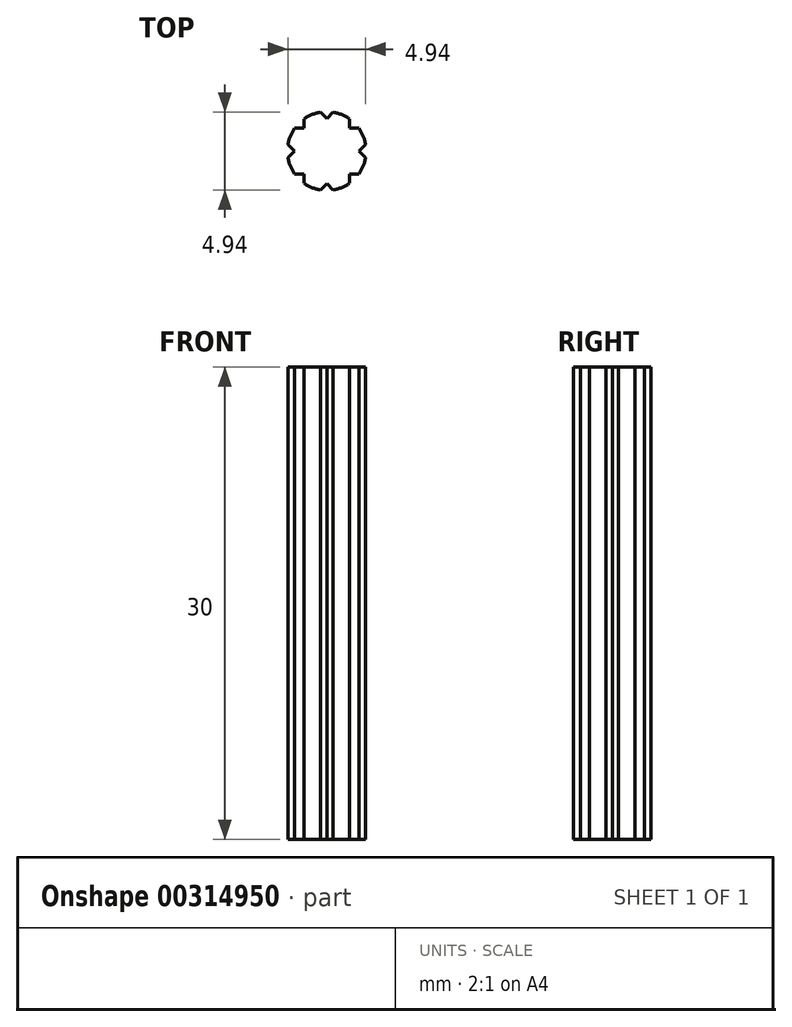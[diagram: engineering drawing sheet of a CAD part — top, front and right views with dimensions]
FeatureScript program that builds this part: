
annotation { "Feature Type Name" : "Feature", "Feature Type Description" : "" }
export const myFeature = defineFeature(function(context is Context, id is Id, definition is map)
    precondition{}
    {
        {
            assignVariable(context, id + "F0", {"name" : "height", "anyValue" : 30});
        }
        {
            assignVariable(context, id + "F1", {"name" : "notches", "anyValue" : 8});
        }
        {
            var Q0;
            Q0=qCreatedBy(makeId("Top.planeOp"),FACE);
            var sketch = newSketch(context, id + "F2", { "sketchPlane" : qUnion([Q0])});
            skCircle(sketch, "E0", {"center": v(0, 0) * mm, "radius": 2.5 * mm});
            skLineSegment(sketch, "E1", {"start": v(0, 0) * mm, "end": v(0, 2.5) * mm, "construction": true});
            skPoint(sketch, "E2.middle", {"position": v(0, 2.5) * mm});
            skSolve(sketch);
        }
        {
            var Q0;
            Q0=qCreatedBy(makeId("Top.planeOp"),FACE);
            var sketch = newSketch(context, id + "F3", { "sketchPlane" : qUnion([Q0])});
            skCircle(sketch, "E3", {"center": v(0, 0) * mm, "radius": 2.5 * mm});
            skLineSegment(sketch, "E4", {"start": v(0, 0) * mm, "end": v(0, 2.5) * mm, "construction": true});
            skLineSegment(sketch, "E5.bottom", {"start": v(0.44, 2.5) * mm, "end": v(0, 2.06) * mm});
            skLineSegment(sketch, "E5.top", {"start": v(0, 2.94) * mm, "end": v(-0.44, 2.5) * mm});
            skLineSegment(sketch, "E5.left", {"start": v(0.44, 2.5) * mm, "end": v(0, 2.94) * mm});
            skLineSegment(sketch, "E5.right", {"start": v(0, 2.06) * mm, "end": v(-0.44, 2.5) * mm});
            skPoint(sketch, "E5.middle", {"position": v(0, 2.5) * mm});
            skLineSegment(sketch, "E6", {"start": v(-0.44, 2.5) * mm, "end": v(0.44, 2.5) * mm});
            skSolve(sketch);
        }
        {
            var Q0;
            Q0 = qSketchRegion(id + "F2", true);
            extrude(context, id + "F4", {"entities" : qUnion([Q0]), "offsetDistance" : 25 * mm, "depth" : (getVariable(context, 'height')) * mm});
        }
        {
            var Q0;
            {var subQ0=sQuery(id+"F3.wireOp",EDGE,"E5.bottom");var subQ1=sQuery(id+"F3.wireOp",EDGE,"E3");var subQ2=makeQuery(id+"F3.imprint","INTERSECT",VERTEX,{"derivedFrom":[subQ1,subQ0]});Q0=makeQuery(id+"F3.imprint","IMPRINT",FACE,{"disambiguationData":[TD([[makeQuery(id+"F3.imprint","IMPRINT",EDGE,{"disambiguationData":[TD([[subQ2,-1.0]])],"derivedFrom":subQ1}),1.0]])]});}
            extrude(context, id + "F5", {"entities" : qUnion([Q0]), "oppositeDirection" : true, "offsetDistance" : 25 * mm, "depth" : -(getVariable(context, 'height')) * mm});
        }
        {
            var Q0;
            Q0=makeQuery(id+"F5.opExtrude","SWEPT_BODY",BODY,{"disambiguationData":[OSD([sQuery(id+"F3.wireOp",EDGE,"E3"),sQuery(id+"F3.wireOp",EDGE,"E5.bottom"),sQuery(id+"F3.wireOp",EDGE,"E5.right")])]});
            var Q1;
            Q1=sQuery(id+"F2.wireOp",EDGE,"E0");
            circularPattern(context, id + "F6", {"operationType" : NewBodyOperationType.REMOVE, "entities" : qUnion([Q0]), "axis" : qUnion([Q1]), "angle" : 360 * degree, "instanceCount" : getVariable(context, 'notches'), "equalSpace" : true});
        }
    });
